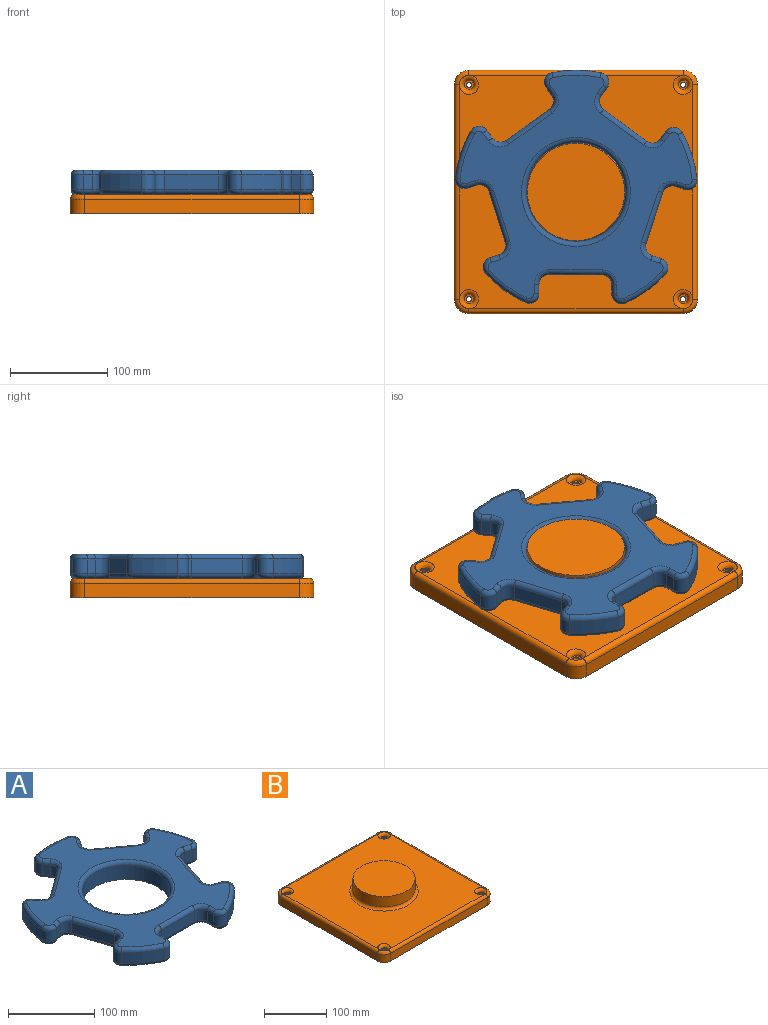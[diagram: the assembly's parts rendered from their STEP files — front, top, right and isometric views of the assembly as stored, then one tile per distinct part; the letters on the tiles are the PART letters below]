
ASSEMBLY  parts=2 mates=1
PART A: 124 faces, bbox 268.9x258.5x25 mm
  f0: plane 238.57x229.73mm, normal (0,0,1), area 19825mm2, adj f83,f84,f85,f86,f87,f88,f89,f90
  f1: plane 238.57x229.73mm, normal (0,0,-1), area 21505.7mm2, adj f6,f43,f44,f45,f46,f47,f48,f49
  f2: cylinder r=125mm len=47.82mm, axis (0,0,-1), area 759.5mm2, adj f34,f42,f82,f113
  f3: cylinder r=125mm len=50.29mm, axis (0,0,-1), area 759.5mm2, adj f27,f35,f67,f97
  f4: cylinder r=125mm len=47.82mm, axis (0,0,-1), area 759.5mm2, adj f20,f28,f51,f84
  f5: cylinder r=125mm len=40.68mm, axis (0,0,-1), area 759.5mm2, adj f13,f21,f50,f100
  f6: cylinder r=51mm len=102mm, axis (0,0,-1), area 6408.8mm2, adj f1,f123
  f7: cylinder r=125mm len=40.68mm, axis (0,0,-1), area 759.5mm2, adj f14,f41,f66,f116
  f8: plane 15x9.73mm, normal (-1,0,0), area 146mm2, adj f11,f14,f62,f112
  f9: plane 55x15mm, normal (0,-1,0), area 825mm2, adj f11,f12,f58,f108
  f10: plane 15x9.73mm, normal (1,0,0), area 146mm2, adj f12,f13,f54,f104
  f11: cylinder r=10mm len=15mm, axis (0,0,-1), area 235.6mm2, adj f8,f9,f60,f110
  f12: cylinder r=10mm len=15mm, axis (0,0,-1), area 235.6mm2, adj f9,f10,f56,f106
  f13: cylinder r=10mm len=15mm, axis (0,0,-1), area 299.5mm2, adj f5,f10,f52,f102
  f14: cylinder r=10mm len=15mm, axis (0,0,-1), area 299.5mm2, adj f7,f8,f64,f114
  f15: plane 15x9.26mm, normal (-0.31,0.95,0), area 146mm2, adj f18,f21,f46,f96
  f16: plane 52.31x17mm, normal (-0.95,-0.31,0), area 825mm2, adj f18,f19,f43,f92
  f17: plane 15x9.26mm, normal (0.31,-0.95,0), area 146mm2, adj f19,f20,f47,f88
  f18: cylinder r=10mm len=15mm, axis (0,0,-1), area 235.6mm2, adj f15,f16,f44,f94
  f19: cylinder r=10mm len=15mm, axis (0,0,-1), area 235.6mm2, adj f16,f17,f45,f90
  f20: cylinder r=10mm len=15mm, axis (0,0,-1), area 299.5mm2, adj f4,f17,f49,f86
  f21: cylinder r=10mm len=16.25mm, axis (0,0,-1), area 299.5mm2, adj f5,f15,f48,f98
  f22: plane 15x7.87mm, normal (0.81,0.59,0), area 146mm2, adj f25,f28,f55,f85
  f23: plane 44.5x32.33mm, normal (-0.59,0.81,0), area 825mm2, adj f25,f26,f59,f89
  f24: plane 15x7.87mm, normal (-0.81,-0.59,0), area 146mm2, adj f26,f27,f63,f93
  f25: cylinder r=10mm len=15mm, axis (0,0,-1), area 235.6mm2, adj f22,f23,f57,f87
  f26: cylinder r=10mm len=15mm, axis (0,0,-1), area 235.6mm2, adj f23,f24,f61,f91
  f27: cylinder r=10mm len=15.67mm, axis (0,0,-1), area 299.5mm2, adj f3,f24,f65,f95
  f28: cylinder r=10mm len=16.78mm, axis (0,0,-1), area 299.5mm2, adj f4,f22,f53,f83
  f29: plane 15x7.87mm, normal (0.81,-0.59,0), area 146mm2, adj f32,f35,f71,f101
  f30: plane 44.5x32.33mm, normal (0.59,0.81,0), area 825mm2, adj f32,f33,f75,f105
  f31: plane 15x7.87mm, normal (-0.81,0.59,0), area 146mm2, adj f33,f34,f79,f109
  f32: cylinder r=10mm len=15mm, axis (0,0,-1), area 235.6mm2, adj f29,f30,f73,f103
  f33: cylinder r=10mm len=15mm, axis (0,0,-1), area 235.6mm2, adj f30,f31,f77,f107
  f34: cylinder r=10mm len=16.78mm, axis (0,0,-1), area 299.5mm2, adj f2,f31,f81,f111
  f35: cylinder r=10mm len=15.67mm, axis (0,0,-1), area 299.5mm2, adj f3,f29,f69,f99
  f36: plane 15x9.26mm, normal (-0.31,-0.95,0), area 146mm2, adj f39,f42,f78,f117
  f37: plane 52.31x17mm, normal (0.95,-0.31,0), area 825mm2, adj f39,f40,f74,f121
  f38: plane 15x9.26mm, normal (0.31,0.95,0), area 146mm2, adj f40,f41,f70,f120
  f39: cylinder r=10mm len=15mm, axis (0,0,-1), area 235.6mm2, adj f36,f37,f76,f119
  f40: cylinder r=10mm len=15mm, axis (0,0,-1), area 235.6mm2, adj f37,f38,f72,f122
  f41: cylinder r=10mm len=16.25mm, axis (0,0,-1), area 299.5mm2, adj f7,f38,f68,f118
  f42: cylinder r=10mm len=15mm, axis (0,0,-1), area 299.5mm2, adj f2,f36,f80,f115
  f43: cylinder r=5mm len=53.85mm, axis (-0.31,0.95,0), area 432mm2, adj f1,f16,f44,f45
  f44: torus R=15mm, axis (0,0,1), area 145.8mm2, adj f1,f18,f43,f46
  f45: torus R=15mm, axis (0,0,1), area 145.8mm2, adj f1,f19,f43,f47
  f46: cylinder r=5mm len=10.8mm, axis (0.95,0.31,0), area 76.4mm2, adj f1,f15,f44,f48
  f47: cylinder r=5mm len=10.8mm, axis (-0.95,-0.31,0), area 76.4mm2, adj f1,f17,f45,f49
  f48: torus R=5mm, axis (0,0,1), area 128.3mm2, adj f1,f21,f46,f50
  f49: torus R=5mm, axis (0,0,1), area 128.3mm2, adj f1,f20,f47,f51
  f50: torus R=120mm, axis (0,0,1), area 391.9mm2, adj f1,f5,f48,f52
  f51: torus R=120mm, axis (0,0,1), area 391.9mm2, adj f1,f4,f49,f53
  f52: torus R=5mm, axis (0,0,1), area 128.3mm2, adj f1,f13,f50,f54
  f53: torus R=5mm, axis (0,0,1), area 128.3mm2, adj f1,f28,f51,f55
  f54: cylinder r=5mm len=9.73mm, axis (0,-1,0), area 76.4mm2, adj f1,f10,f52,f56
  f55: cylinder r=5mm len=10.81mm, axis (0.59,-0.81,0), area 76.4mm2, adj f1,f22,f53,f57
  f56: torus R=15mm, axis (0,0,1), area 145.8mm2, adj f1,f12,f54,f58
  f57: torus R=15mm, axis (0,0,1), area 145.8mm2, adj f1,f25,f55,f59
  f58: cylinder r=5mm len=55mm, axis (-1,0,0), area 432mm2, adj f1,f9,f56,f60
  f59: cylinder r=5mm len=47.44mm, axis (0.81,0.59,0), area 432mm2, adj f1,f23,f57,f61
  f60: torus R=15mm, axis (0,0,1), area 145.8mm2, adj f1,f11,f58,f62
  f61: torus R=15mm, axis (0,0,1), area 145.8mm2, adj f1,f26,f59,f63
  f62: cylinder r=5mm len=9.73mm, axis (0,1,0), area 76.4mm2, adj f1,f8,f60,f64
  f63: cylinder r=5mm len=10.81mm, axis (-0.59,0.81,0), area 76.4mm2, adj f1,f24,f61,f65
  f64: torus R=5mm, axis (0,0,1), area 128.3mm2, adj f1,f14,f62,f66
  f65: torus R=5mm, axis (0,0,1), area 128.3mm2, adj f1,f27,f63,f67
  f66: torus R=120mm, axis (0,0,1), area 391.9mm2, adj f1,f7,f64,f68
  f67: torus R=120mm, axis (0,0,1), area 391.9mm2, adj f1,f3,f65,f69
  f68: torus R=5mm, axis (0,0,1), area 128.3mm2, adj f1,f41,f66,f70
  f69: torus R=5mm, axis (0,0,1), area 128.3mm2, adj f1,f35,f67,f71
  f70: cylinder r=5mm len=10.8mm, axis (0.95,-0.31,0), area 76.4mm2, adj f1,f38,f68,f72
  f71: cylinder r=5mm len=10.81mm, axis (-0.59,-0.81,0), area 76.4mm2, adj f1,f29,f69,f73
  f72: torus R=15mm, axis (0,0,1), area 145.8mm2, adj f1,f40,f70,f74
  f73: torus R=15mm, axis (0,0,1), area 145.8mm2, adj f1,f32,f71,f75
  f74: cylinder r=5mm len=53.85mm, axis (-0.31,-0.95,0), area 432mm2, adj f1,f37,f72,f76
  f75: cylinder r=5mm len=47.44mm, axis (0.81,-0.59,0), area 432mm2, adj f1,f30,f73,f77
  f76: torus R=15mm, axis (0,0,1), area 145.8mm2, adj f1,f39,f74,f78
  f77: torus R=15mm, axis (0,0,1), area 145.8mm2, adj f1,f33,f75,f79
  f78: cylinder r=5mm len=10.8mm, axis (-0.95,0.31,0), area 76.4mm2, adj f1,f36,f76,f80
  f79: cylinder r=5mm len=10.81mm, axis (0.59,0.81,0), area 76.4mm2, adj f1,f31,f77,f81
  f80: torus R=5mm, axis (0,0,1), area 128.3mm2, adj f1,f42,f78,f82
  f81: torus R=5mm, axis (0,0,1), area 128.3mm2, adj f1,f34,f79,f82
  f82: torus R=120mm, axis (0,0,1), area 391.9mm2, adj f1,f2,f80,f81
  f83: torus R=5mm, axis (0,0,1), area 128.3mm2, adj f0,f28,f84,f85
  f84: torus R=120mm, axis (0,0,1), area 391.9mm2, adj f0,f4,f83,f86
  f85: cylinder r=5mm len=10.81mm, axis (-0.59,0.81,0), area 76.4mm2, adj f0,f22,f83,f87
  f86: torus R=5mm, axis (0,0,1), area 128.3mm2, adj f0,f20,f84,f88
  f87: torus R=15mm, axis (0,0,1), area 145.8mm2, adj f0,f25,f85,f89
  f88: cylinder r=5mm len=10.8mm, axis (0.95,0.31,0), area 76.4mm2, adj f0,f17,f86,f90
  f89: cylinder r=5mm len=47.44mm, axis (-0.81,-0.59,0), area 432mm2, adj f0,f23,f87,f91
  f90: torus R=15mm, axis (0,0,1), area 145.8mm2, adj f0,f19,f88,f92
  f91: torus R=15mm, axis (0,0,1), area 145.8mm2, adj f0,f26,f89,f93
  f92: cylinder r=5mm len=53.85mm, axis (0.31,-0.95,0), area 432mm2, adj f0,f16,f90,f94
  f93: cylinder r=5mm len=10.81mm, axis (0.59,-0.81,0), area 76.4mm2, adj f0,f24,f91,f95
  f94: torus R=15mm, axis (0,0,1), area 145.8mm2, adj f0,f18,f92,f96
  f95: torus R=5mm, axis (0,0,1), area 128.3mm2, adj f0,f27,f93,f97
  f96: cylinder r=5mm len=10.8mm, axis (-0.95,-0.31,0), area 76.4mm2, adj f0,f15,f94,f98
  f97: torus R=120mm, axis (0,0,1), area 391.9mm2, adj f0,f3,f95,f99
  f98: torus R=5mm, axis (0,0,1), area 128.3mm2, adj f0,f21,f96,f100
  f99: torus R=5mm, axis (0,0,1), area 128.3mm2, adj f0,f35,f97,f101
  f100: torus R=120mm, axis (0,0,1), area 391.9mm2, adj f0,f5,f98,f102
  f101: cylinder r=5mm len=10.81mm, axis (0.59,0.81,0), area 76.4mm2, adj f0,f29,f99,f103
  f102: torus R=5mm, axis (0,0,1), area 128.3mm2, adj f0,f13,f100,f104
  f103: torus R=15mm, axis (0,0,1), area 145.8mm2, adj f0,f32,f101,f105
  f104: cylinder r=5mm len=9.73mm, axis (0,1,0), area 76.4mm2, adj f0,f10,f102,f106
  f105: cylinder r=5mm len=47.44mm, axis (-0.81,0.59,0), area 432mm2, adj f0,f30,f103,f107
  f106: torus R=15mm, axis (0,0,1), area 145.8mm2, adj f0,f12,f104,f108
  f107: torus R=15mm, axis (0,0,1), area 145.8mm2, adj f0,f33,f105,f109
  f108: cylinder r=5mm len=55mm, axis (1,0,0), area 432mm2, adj f0,f9,f106,f110
  f109: cylinder r=5mm len=10.81mm, axis (-0.59,-0.81,0), area 76.4mm2, adj f0,f31,f107,f111
  f110: torus R=15mm, axis (0,0,1), area 145.8mm2, adj f0,f11,f108,f112
  f111: torus R=5mm, axis (0,0,1), area 128.3mm2, adj f0,f34,f109,f113
  f112: cylinder r=5mm len=9.73mm, axis (0,-1,0), area 76.4mm2, adj f0,f8,f110,f114
  f113: torus R=120mm, axis (0,0,1), area 391.9mm2, adj f0,f2,f111,f115
  f114: torus R=5mm, axis (0,0,1), area 128.3mm2, adj f0,f14,f112,f116
  f115: torus R=5mm, axis (0,0,1), area 128.3mm2, adj f0,f42,f113,f117
  f116: torus R=120mm, axis (0,0,1), area 391.9mm2, adj f0,f7,f114,f118
  f117: cylinder r=5mm len=10.8mm, axis (0.95,-0.31,0), area 76.4mm2, adj f0,f36,f115,f119
  f118: torus R=5mm, axis (0,0,1), area 128.3mm2, adj f0,f41,f116,f120
  f119: torus R=15mm, axis (0,0,1), area 145.8mm2, adj f0,f39,f117,f121
  f120: cylinder r=5mm len=10.8mm, axis (-0.95,0.31,0), area 76.4mm2, adj f0,f38,f118,f122
  f121: cylinder r=5mm len=53.85mm, axis (0.31,0.95,0), area 432mm2, adj f0,f37,f119,f122
  f122: torus R=15mm, axis (0,0,1), area 145.8mm2, adj f0,f40,f120,f121
  f123: torus R=56mm, axis (0,0,1), area 2606.4mm2, adj f0,f6
PART B: 33 faces, bbox 252.5x252.5x45 mm
  f0: plane 220x15mm, normal (1,0,0), area 3300mm2, adj f5,f8,f11,f29
  f1: plane 220x15mm, normal (0,1,0), area 3300mm2, adj f5,f8,f9,f30
  f2: plane 220x15mm, normal (-1,0,0), area 3300mm2, adj f5,f9,f10,f26
  f3: plane 220x15mm, normal (0,-1,0), area 3300mm2, adj f5,f10,f11,f25
  f4: plane 240x240mm, normal (0,0,1), area 46785.4mm2, adj f20,f21,f22,f23,f24,f25,f26,f27
  f5: plane 250x250mm, normal (0,0,-1), area 62211.8mm2, adj f0,f1,f2,f3,f8,f9,f10,f11
  f6: cylinder r=50mm len=100mm, axis (0,0,-1), area 6283.2mm2, adj f7,f32
  f7: plane 100x100mm, normal (0,0,1), area 7854mm2, adj f6
  f8: cylinder r=15mm len=15mm, axis (0,0,-1), area 353.4mm2, adj f0,f1,f5,f31
  f9: cylinder r=15mm len=15mm, axis (0,0,1), area 353.4mm2, adj f1,f2,f5,f28
  f10: cylinder r=15mm len=15mm, axis (0,0,-1), area 353.4mm2, adj f2,f3,f5,f24
  f11: cylinder r=15mm len=15mm, axis (0,0,1), area 353.4mm2, adj f0,f3,f5,f27
  f12: cylinder r=2.75mm len=15mm, axis (0,0,1), area 259.2mm2, adj f5,f13
  f13: plane 9.75x9.75mm, normal (0,0,1), area 50.9mm2, adj f12,f23
  f14: cylinder r=2.75mm len=15mm, axis (0,0,1), area 259.2mm2, adj f5,f15
  f15: plane 9.75x9.75mm, normal (0,0,1), area 50.9mm2, adj f14,f22
  f16: cylinder r=2.75mm len=15mm, axis (0,0,1), area 259.2mm2, adj f5,f17
  f17: plane 9.75x9.75mm, normal (0,0,1), area 50.9mm2, adj f16,f21
  f18: cylinder r=2.75mm len=15mm, axis (0,0,1), area 259.2mm2, adj f5,f19
  f19: plane 9.75x9.75mm, normal (0,0,1), area 50.9mm2, adj f18,f20
  f20: torus R=9.88mm, axis (0,0,1), area 330.2mm2, adj f4,f19
  f21: torus R=9.88mm, axis (0,0,1), area 330.2mm2, adj f4,f17
  f22: torus R=9.88mm, axis (0,0,1), area 330.2mm2, adj f4,f15
  f23: torus R=9.88mm, axis (0,0,1), area 330.2mm2, adj f4,f13
  f24: torus R=10mm, axis (0,0,1), area 162.6mm2, adj f4,f10,f25,f26
  f25: cylinder r=5mm len=220mm, axis (-1,0,0), area 1727.9mm2, adj f3,f4,f24,f27
  f26: cylinder r=5mm len=220mm, axis (0,1,0), area 1727.9mm2, adj f2,f4,f24,f28
  f27: torus R=10mm, axis (0,0,1), area 162.6mm2, adj f4,f11,f25,f29
  f28: torus R=10mm, axis (0,0,1), area 162.6mm2, adj f4,f9,f26,f30
  f29: cylinder r=5mm len=220mm, axis (0,-1,0), area 1727.9mm2, adj f0,f4,f27,f31
  f30: cylinder r=5mm len=220mm, axis (1,0,0), area 1727.9mm2, adj f1,f4,f28,f31
  f31: torus R=10mm, axis (0,0,1), area 162.6mm2, adj f4,f8,f29,f30
  f32: torus R=55mm, axis (0,0,1), area 2557.1mm2, adj f4,f6
PLACE A rot(axis=(0,0,-1),144.3deg) t=(-5.76,-14.1,-38.67)mm
PLACE B t=(-5.76,-14.1,-38.67)mm fixed
MATE revolute A.f2 <-> B.f6  axis (0,0,1) through (-5.76,-14.1,6.33)mm
